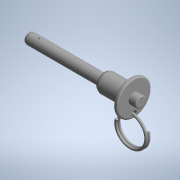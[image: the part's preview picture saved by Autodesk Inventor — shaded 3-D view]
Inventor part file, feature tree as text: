
AUTODESK INVENTOR PART (.ipt)
format: ipt  version: 2022.3 (Build 263350000, 350)  size: 298,496 bytes
history: native  units: mm (DEFAULTED — no unit token found)
features: mirror x2, revolve x1, other x1, sweep x1
ambient origin geometry x8: Origin, YZ Plane, XZ Plane, XY Plane, X Axis, Y Axis, Z Axis, Center Point
bodies: Solid1 (feature_tree), Solid2 (feature_tree), Solid3 (feature_tree), Solid4 (feature_tree), Solid5 (feature_tree)
feature tree (5):
  revolve  "Revolve2"  [1 undecoded]
  mirror  "Mirror2"
  mirror  "Mirror1[1]"
  other  "Cut-Extrude1"
  sweep  "Sweep2"
note: 1 required parameter value undecoded (feature->parameter linkage not recoverable at this tier; creation-order binding heuristic only, values carry confidence <= 0.55)
